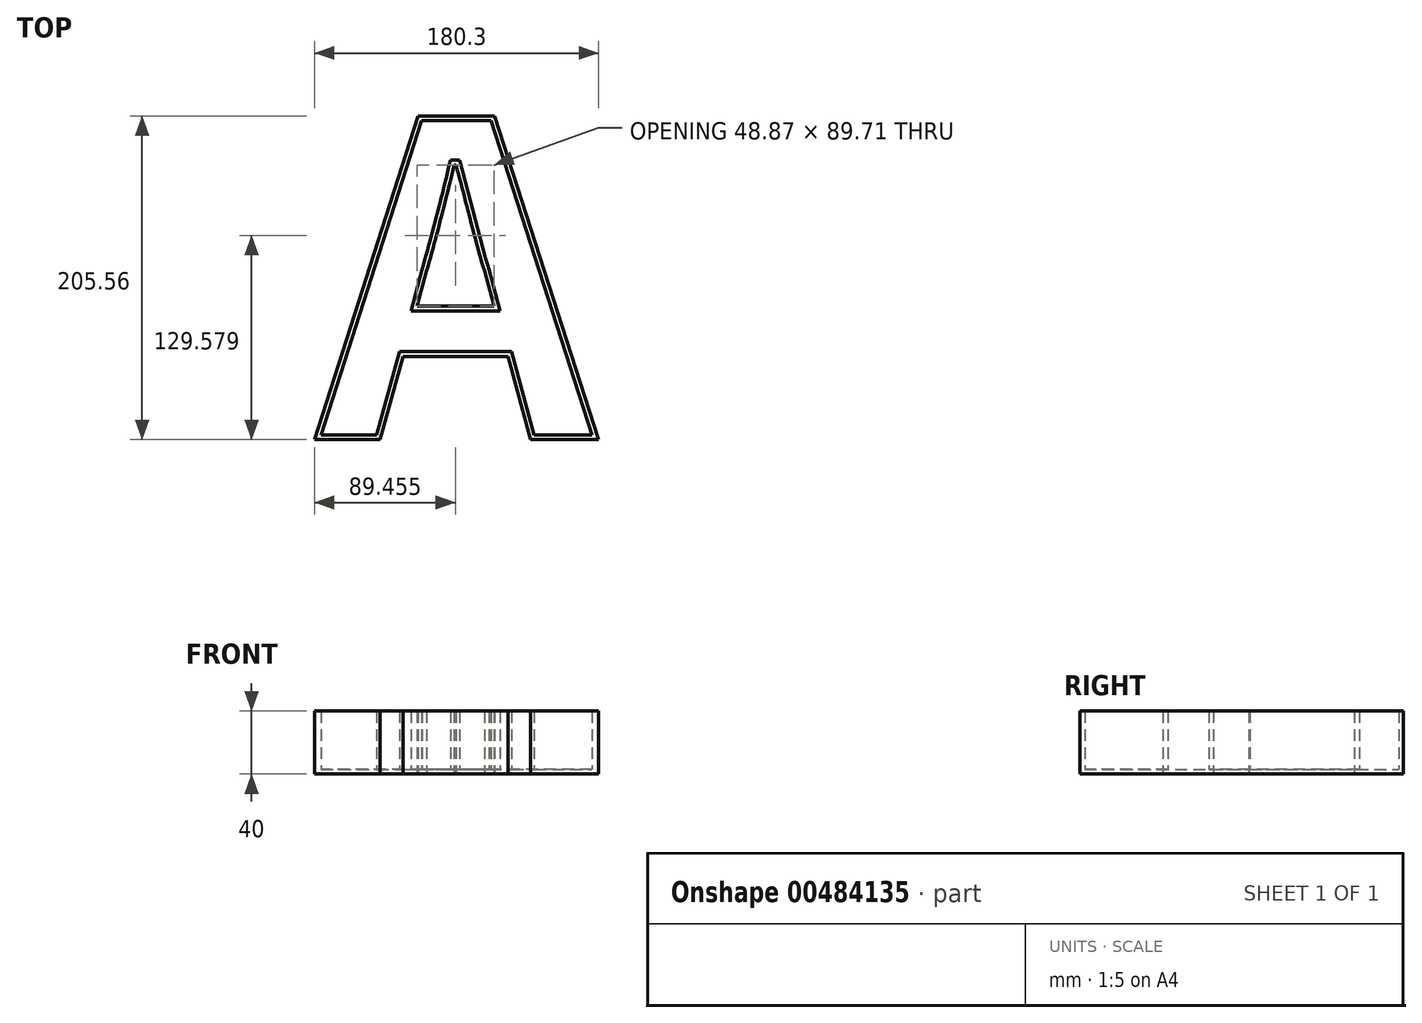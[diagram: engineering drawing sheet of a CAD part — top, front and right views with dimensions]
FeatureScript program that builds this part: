
annotation { "Feature Type Name" : "Feature", "Feature Type Description" : "" }
export const myFeature = defineFeature(function(context is Context, id is Id, definition is map)
    precondition{}
    {
        {
            var Q0;
            Q0=qCreatedBy(makeId("Top.planeOp"),FACE);
            var sketch = newSketch(context, id + "F0", { "sketchPlane" : qUnion([Q0])});
            skText(sketch, "E0", { "text": "A", "fontName": "NotoSansCJKkr-Bold.otf"});
            const initialGuessF0  = {"E0": [-0.1071, -0.0948, 1, 0, 0.2]};
            skSetInitialGuess(sketch, initialGuessF0);
            skSolve(sketch);
        }
        {
            var Q0;
            Q0 = qSketchRegion(id + "F0", true);
            extrude(context, id + "F1", {"entities" : qUnion([Q0]), "depth" : 40 * mm});
        }
        {
            var Q0;
            Q0=makeQuery(id+"F1.opExtrude","CAP_FACE",FACE,{"disambiguationData":[OSD([sQuery(id+"F0.wireOp",EDGE,"E0.sketch_text.stroke-0"),sQuery(id+"F0.wireOp",EDGE,"E0.sketch_text.stroke-1"),sQuery(id+"F0.wireOp",EDGE,"E0.sketch_text.stroke-2"),sQuery(id+"F0.wireOp",EDGE,"E0.sketch_text.stroke-3"),sQuery(id+"F0.wireOp",EDGE,"E0.sketch_text.stroke-4"),sQuery(id+"F0.wireOp",EDGE,"E0.sketch_text.stroke-5"),sQuery(id+"F0.wireOp",EDGE,"E0.sketch_text.stroke-6"),sQuery(id+"F0.wireOp",EDGE,"E0.sketch_text.stroke-7"),sQuery(id+"F0.wireOp",EDGE,"E0.sketch_text.stroke-8"),sQuery(id+"F0.wireOp",EDGE,"E0.sketch_text.stroke-9"),sQuery(id+"F0.wireOp",EDGE,"E0.sketch_text.stroke-10"),sQuery(id+"F0.wireOp",EDGE,"E0.sketch_text.stroke-11"),sQuery(id+"F0.wireOp",EDGE,"E0.sketch_text.stroke-12"),sQuery(id+"F0.wireOp",EDGE,"E0.sketch_text.stroke-13")])],"isStart":false});
            shell(context, id + "F2", {"entities" : qUnion([Q0]), "thickness" : 3 * mm});
        }
    });
